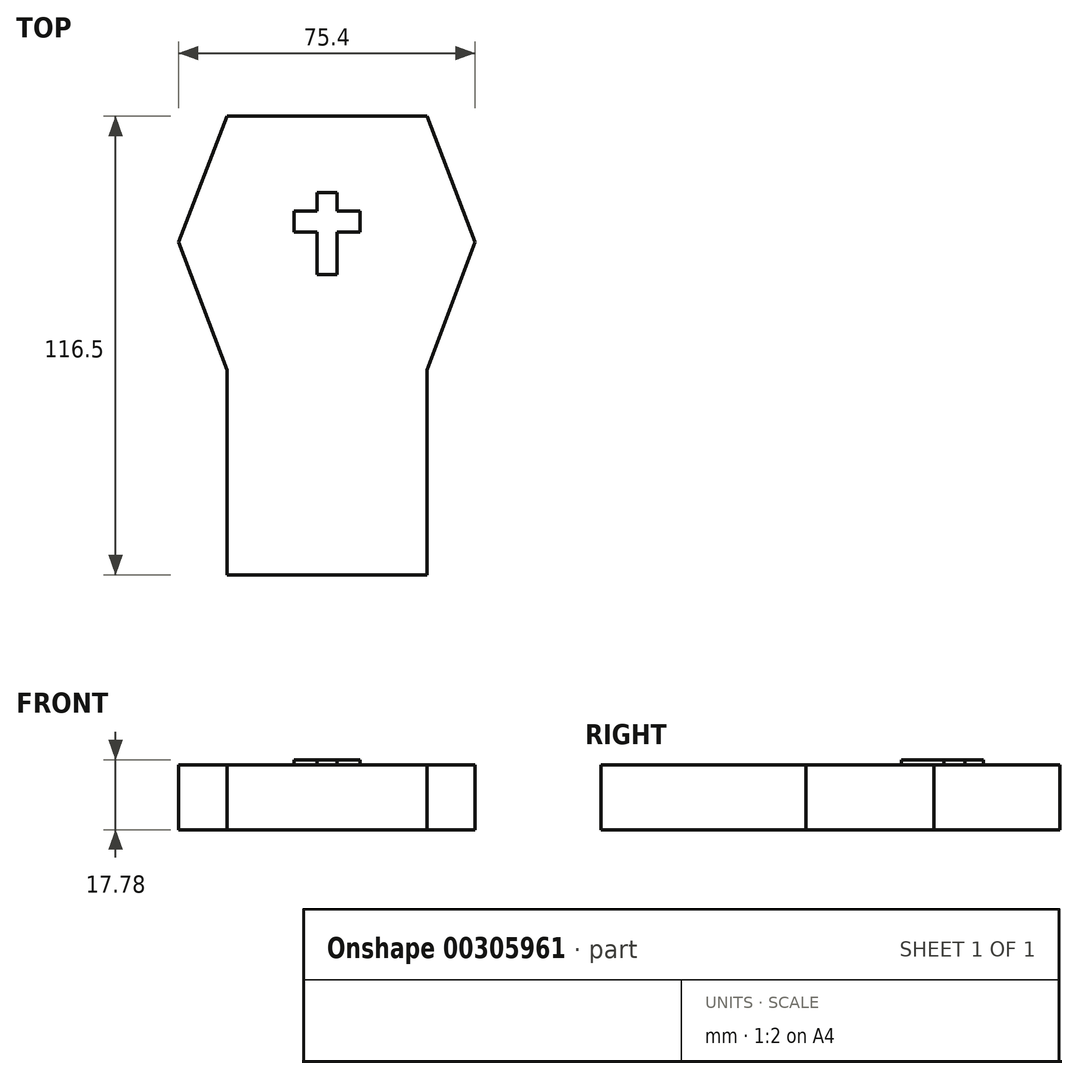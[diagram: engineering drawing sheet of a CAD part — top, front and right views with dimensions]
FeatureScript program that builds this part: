
annotation { "Feature Type Name" : "Feature", "Feature Type Description" : "" }
export const myFeature = defineFeature(function(context is Context, id is Id, definition is map)
    precondition{}
    {
        {
            var Q0;
            Q0=qCreatedBy(makeId("Top.planeOp"),FACE);
            var sketch = newSketch(context, id + "F0", { "sketchPlane" : qUnion([Q0])});
            skLineSegment(sketch, "E0", {"start": v(0, -68.15) * mm, "end": v(-25.4, -68.15) * mm});
            skLineSegment(sketch, "E1", {"start": v(-25.4, -68.15) * mm, "end": v(0, -68.15) * mm});
            skLineSegment(sketch, "E2", {"start": v(0, -68.15) * mm, "end": v(25.4, -68.15) * mm});
            skLineSegment(sketch, "E3", {"start": v(-25.4, -68.15) * mm, "end": v(-25.4, -16.12) * mm});
            skLineSegment(sketch, "E4", {"start": v(25.4, -68.15) * mm, "end": v(25.4, -16.12) * mm});
            skLineSegment(sketch, "E5", {"start": v(25.4, -16.12) * mm, "end": v(37.7, 16.4) * mm});
            skLineSegment(sketch, "E6", {"start": v(37.7, 16.4) * mm, "end": v(25.4, 48.35) * mm});
            skLineSegment(sketch, "E7", {"start": v(0, -68.15) * mm, "end": v(0, 67.06) * mm, "construction": true});
            skLineSegment(sketch, "E8.MirrorCS", {"start": v(-25.4, -16.12) * mm, "end": v(-37.7, 16.4) * mm});
            skLineSegment(sketch, "E9.MirrorCS", {"start": v(-37.7, 16.4) * mm, "end": v(-25.4, 48.35) * mm});
            skLineSegment(sketch, "E10", {"start": v(-25.4, 48.35) * mm, "end": v(25.4, 48.35) * mm});
            skSolve(sketch);
        }
        {
            var Q0;
            Q0 = qSketchRegion(id + "F0", true);
            extrude(context, id + "F1", {"entities" : qUnion([Q0]), "depth" : 16.5 * mm});
        }
        {
            var Q0;
            Q0=makeQuery(id+"F1.opExtrude","CAP_FACE",FACE,{"disambiguationData":[OSD([sQuery(id+"F0.wireOp",EDGE,"E1"),sQuery(id+"F0.wireOp",EDGE,"E2"),sQuery(id+"F0.wireOp",EDGE,"E3"),sQuery(id+"F0.wireOp",EDGE,"E4"),sQuery(id+"F0.wireOp",EDGE,"E5"),sQuery(id+"F0.wireOp",EDGE,"E6"),sQuery(id+"F0.wireOp",EDGE,"E8.MirrorCS"),sQuery(id+"F0.wireOp",EDGE,"E9.MirrorCS"),sQuery(id+"F0.wireOp",EDGE,"E10")])],"isStart":false});
            var sketch = newSketch(context, id + "F2", { "sketchPlane" : qUnion([Q0])});
            skLineSegment(sketch, "E11", {"start": v(0, 8.16) * mm, "end": v(-2.54, 8.16) * mm});
            skLineSegment(sketch, "E12", {"start": v(-2.54, 8.16) * mm, "end": v(-2.54, 18.87) * mm});
            skLineSegment(sketch, "E13", {"start": v(0, 8.16) * mm, "end": v(2.54, 8.16) * mm});
            skLineSegment(sketch, "E14", {"start": v(2.54, 8.16) * mm, "end": v(2.54, 18.87) * mm});
            skLineSegment(sketch, "E15", {"start": v(-2.54, 18.87) * mm, "end": v(-8.37, 18.87) * mm});
            skLineSegment(sketch, "E16", {"start": v(-8.37, 18.87) * mm, "end": v(-8.37, 24.25) * mm});
            skLineSegment(sketch, "E17", {"start": v(-8.37, 24.25) * mm, "end": v(-2.54, 24.25) * mm});
            skLineSegment(sketch, "E18", {"start": v(-2.54, 24.25) * mm, "end": v(-2.54, 28.94) * mm});
            skLineSegment(sketch, "E19", {"start": v(-2.54, 28.94) * mm, "end": v(2.54, 28.94) * mm});
            skLineSegment(sketch, "E20", {"start": v(2.54, 28.94) * mm, "end": v(2.54, 24.25) * mm});
            skLineSegment(sketch, "E21", {"start": v(0, 30.9) * mm, "end": v(0, -5.18) * mm, "construction": true});
            skLineSegment(sketch, "E22.MirrorCS", {"start": v(8.37, 24.25) * mm, "end": v(2.54, 24.25) * mm});
            skLineSegment(sketch, "E23.MirrorCS", {"start": v(8.37, 18.87) * mm, "end": v(8.37, 24.25) * mm});
            skLineSegment(sketch, "E24.MirrorCS", {"start": v(2.54, 18.87) * mm, "end": v(8.37, 18.87) * mm});
            skSolve(sketch);
        }
        {
            var Q0;
            Q0=makeQuery(id+"F2.imprint","IMPRINT",FACE,{"disambiguationData":[TD([[makeQuery(id+"F2.imprint","IMPRINT",EDGE,{"derivedFrom":sQuery(id+"F2.wireOp",EDGE,"E11")}),-1.0]])]});
            extrude(context, id + "F3", {"entities" : qUnion([Q0]), "depth" : 1.27 * mm});
        }
    });
